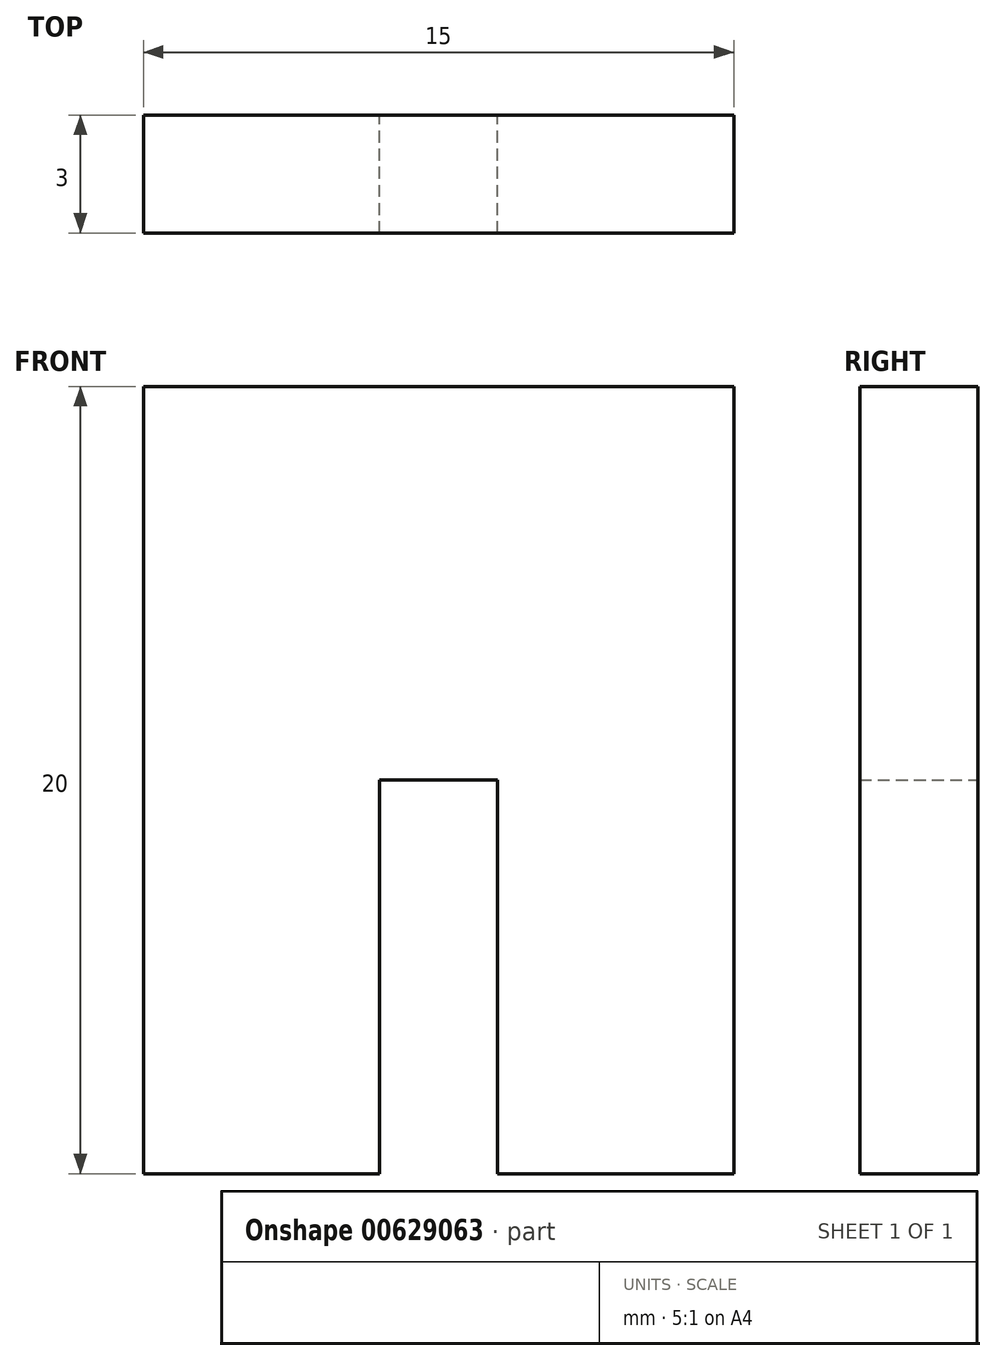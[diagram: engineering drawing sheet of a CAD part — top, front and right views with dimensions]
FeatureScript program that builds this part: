
annotation { "Feature Type Name" : "Feature", "Feature Type Description" : "" }
export const myFeature = defineFeature(function(context is Context, id is Id, definition is map)
    precondition{}
    {
        {
            var Q0;
            Q0=qCreatedBy(makeId("Front.planeOp"),FACE);
            var sketch = newSketch(context, id + "F0", { "sketchPlane" : qUnion([Q0])});
            skLineSegment(sketch, "E0", {"start": v(0, 17.82) * mm, "end": v(0, -20.11) * mm, "construction": true});
            skLineSegment(sketch, "E1.bottom", {"start": v(-7.5, 10) * mm, "end": v(7.5, 10) * mm});
            skLineSegment(sketch, "E1.top", {"start": v(-7.5, -10) * mm, "end": v(-1.5, -10) * mm});
            skLineSegment(sketch, "E1.left", {"start": v(-7.5, 10) * mm, "end": v(-7.5, -10) * mm});
            skLineSegment(sketch, "E1.right", {"start": v(7.5, 10) * mm, "end": v(7.5, -10) * mm});
            skLineSegment(sketch, "E2.top", {"start": v(-1.5, 0) * mm, "end": v(1.5, 0) * mm});
            skLineSegment(sketch, "E2.left", {"start": v(-1.5, -10) * mm, "end": v(-1.5, 0) * mm});
            skLineSegment(sketch, "E2.right", {"start": v(1.5, -10) * mm, "end": v(1.5, 0) * mm});
            skLineSegment(sketch, "E3.trimOffspring", {"start": v(1.5, -10) * mm, "end": v(7.5, -10) * mm});
            skSolve(sketch);
        }
        {
            var Q0;
            Q0 = qSketchRegion(id + "F0", true);
            extrude(context, id + "F1", {"entities" : qUnion([Q0]), "endBound" : BoundingType.SYMMETRIC, "depth" : 3 * mm, "offsetDistance" : 25 * mm});
        }
    });
